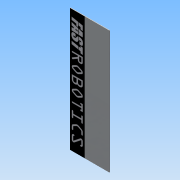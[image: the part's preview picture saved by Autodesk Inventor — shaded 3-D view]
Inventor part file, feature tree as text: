
AUTODESK INVENTOR PART (.ipt)
format: ipt  version: 2014 (Build 180170000, 170)  size: 294,912 bytes
history: native  units: in
note: dims shown in document units (in); Inventor stores cm internally (conversion verified against a paired STEP export)
features: other x2, sketch x2, reference x2, extrude x1
ambient origin geometry x8: Origin, YZ Plane, XZ Plane, XY Plane, X Axis, Y Axis, Z Axis, Center Point
bodies: Solid1 (feature_tree)
feature tree (7):
  extrude  "Extrusion1"  [1 undecoded]
  other  "Decal1"
  sketch  "Sketch1"  dims[d0=0.0625in d1=0.0in]
  reference  "Reference1"
  reference  "Reference2"
  sketch  "Sketch2"
  other  "Image1"
note: 1 required parameter value undecoded (feature->parameter linkage not recoverable at this tier; creation-order binding heuristic only, values carry confidence <= 0.55)
